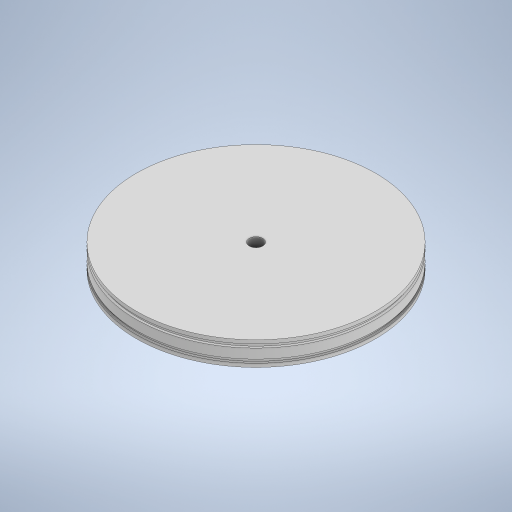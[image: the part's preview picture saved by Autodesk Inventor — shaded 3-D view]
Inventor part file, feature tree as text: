
AUTODESK INVENTOR PART (.ipt)
format: ipt  version: 2023 (Build 270158030, 158C)  size: 269,312 bytes
history: native  units: in
note: dims shown in document units (in); Inventor stores cm internally (conversion verified against a paired STEP export)
features: sketch x4, extrude x2, hole x1, chamfer x1, revolve x1
ambient origin geometry x8: Origin, YZ Plane, XZ Plane, XY Plane, X Axis, Y Axis, Z Axis, Center Point
bodies: Solid1 (feature_tree)
feature tree (9):
  extrude  "Extrusion1"  Depth=0.5in TaperAngle=0.0deg
  hole  "Hole1"  [1 undecoded]
  extrude  "Extrusion2"  Depth=0.172in TaperAngle=45.0deg
  chamfer  "Chamfer1"  Distance=0.075in
  revolve  "Revolution1"  [1 undecoded]
  sketch  "Sketch1"  dims[d0=5.0in d1=0.5in d2=0.0in]
  sketch  "Sketch2"  dims[d3=0.281in d4=0.75in d5=0.75in d6=0.188in d7=0.5635in d8=1.0in d9=0.8108in d10=0.438in]
  sketch  "Sketch3"  dims[d11=0.172in d12=0.0in d13=0.02in d14=0.125in d15=45.0deg]
  sketch  "Sketch4"  dims[d16=0.05in d17=0.075in d18=0.2in d19=90.0deg]
note: 2 required parameter values undecoded (feature->parameter linkage not recoverable at this tier; creation-order binding heuristic only, values carry confidence <= 0.55)